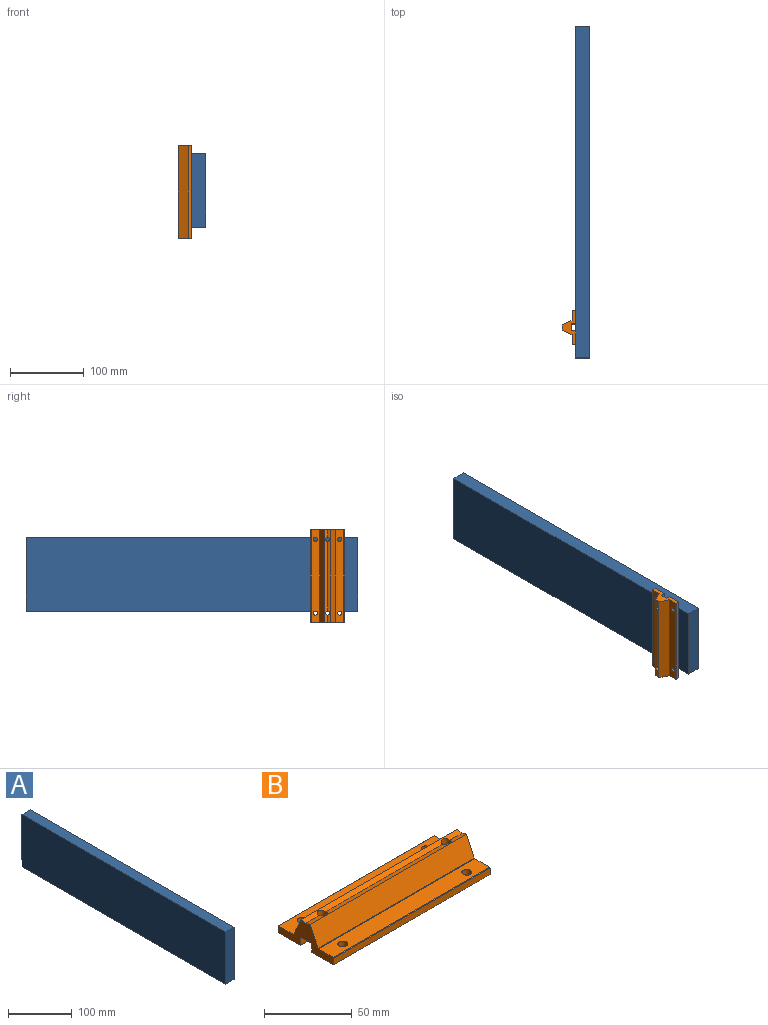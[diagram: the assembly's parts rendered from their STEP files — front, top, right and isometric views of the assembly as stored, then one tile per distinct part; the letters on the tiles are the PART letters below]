
ASSEMBLY  parts=2 mates=2
PART A: 6 faces, bbox 19x450x100 mm
  f0: plane 450x19mm, normal (0,0,1), area 8550mm2, adj f1,f3,f4,f5
  f1: plane 450x100mm, normal (-1,0,0), area 45000mm2, adj f0,f2,f4,f5
  f2: plane 450x19mm, normal (0,0,-1), area 8550mm2, adj f1,f3,f4,f5
  f3: plane 450x100mm, normal (1,0,0), area 45000mm2, adj f0,f2,f4,f5
  f4: plane 100x19mm, normal (0,-1,0), area 1900mm2, adj f0,f1,f2,f3
  f5: plane 100x19mm, normal (0,1,0), area 1900mm2, adj f0,f1,f2,f3
PART B: 25 faces, bbox 126x45x18.8 mm
  f0: plane 126x9.5mm, normal (0,0,-1), area 1149.5mm2, adj f1,f8,f9,f14,f23,f24
  f1: plane 126x6mm, normal (0,-1,0), area 756mm2, adj f0,f2,f23,f24
  f2: plane 126x17.75mm, normal (0,0,-1), area 2189mm2, adj f1,f3,f10,f11,f23,f24
  f3: plane 126x4.5mm, normal (0,1,0), area 567mm2, adj f2,f4,f23,f24
  f4: cylinder r=0.5mm len=126mm, axis (1,0,0), area 99mm2, adj f3,f5,f23,f24
  f5: plane 126x11.74mm, normal (0,0,1), area 1432.2mm2, adj f4,f6,f10,f11,f23,f24
  f6: cylinder r=0.5mm len=126mm, axis (-1,0,0), area 71.5mm2, adj f5,f7,f23,f24
  f7: plane 126x13.52mm, normal (0,0.91,0.42), area 1879.3mm2, adj f6,f22,f23,f24
  f8: cylinder r=2.75mm len=12.57mm, axis (0,0,-1), area 211.7mm2, adj f0,f21,f22
  f9: cylinder r=2.75mm len=12.57mm, axis (0,0,-1), area 211.7mm2, adj f0,f21,f22
  f10: cylinder r=2.75mm len=5.5mm, axis (0,0,-1), area 86.4mm2, adj f2,f5
  f11: cylinder r=2.75mm len=5.5mm, axis (0,0,-1), area 86.4mm2, adj f2,f5
  f12: cylinder r=2.75mm len=5.5mm, axis (0,0,-1), area 86.4mm2, adj f15,f18
  f13: cylinder r=2.75mm len=5.5mm, axis (0,0,-1), area 86.4mm2, adj f15,f18
  f14: plane 126x6mm, normal (0,1,0), area 756mm2, adj f0,f15,f23,f24
  f15: plane 126x17.75mm, normal (0,0,-1), area 2189mm2, adj f12,f13,f14,f16,f23,f24
  f16: plane 126x4.5mm, normal (0,-1,0), area 567mm2, adj f15,f17,f23,f24
  f17: cylinder r=0.5mm len=126mm, axis (1,0,0), area 99mm2, adj f16,f18,f23,f24
  f18: plane 126x11.74mm, normal (0,0,1), area 1432.2mm2, adj f12,f13,f17,f19,f23,f24
  f19: cylinder r=0.5mm len=126mm, axis (-1,0,0), area 71.5mm2, adj f18,f20,f23,f24
  f20: plane 126x13.52mm, normal (0,-0.91,0.42), area 1879.3mm2, adj f19,f21,f23,f24
  f21: plane 126x3.5mm, normal (0,0.3,0.95), area 437.5mm2, adj f8,f9,f20,f22,f23,f24
  f22: plane 126x3.5mm, normal (0,-0.3,0.95), area 437.5mm2, adj f7,f8,f9,f21,f23,f24
  f23: plane 45x18.81mm, normal (1,0,0), area 349.6mm2, adj f0,f1,f2,f3,f4,f5,f6,f7
  f24: plane 45x18.81mm, normal (-1,0,0), area 349.6mm2, adj f0,f1,f2,f3,f4,f5,f6,f7
PLACE A t=(93.59,36.34,63.25)mm fixed
PLACE B rot(axis=(0.71,0,-0.71),180deg) t=(93.59,-147.47,501.68)mm
MATE parallel B.f3 <-> A.f4  axis (0,-1,0) through (91.34,-169.97,201.93)mm
MATE planar B.f13 <-> A.f1  axis (1,0,0) through (93.59,-130.97,151.68)mm
